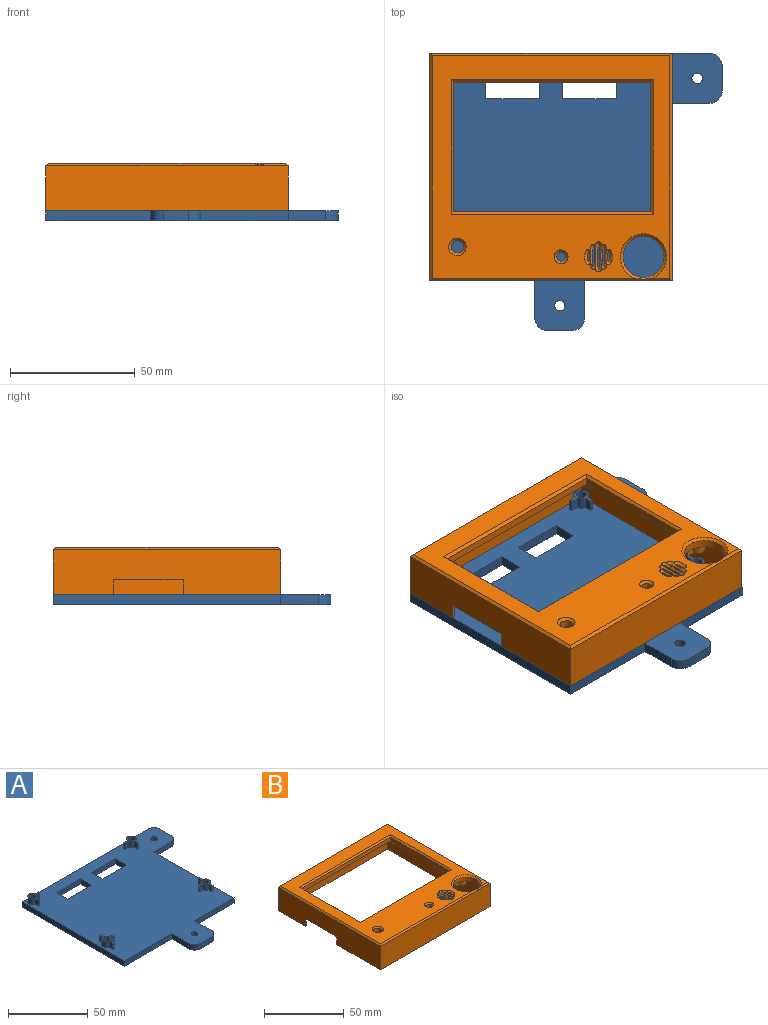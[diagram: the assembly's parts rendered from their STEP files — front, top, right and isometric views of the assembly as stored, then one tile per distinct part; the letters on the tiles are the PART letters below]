
ASSEMBLY  parts=2 mates=1
PART A: 74 faces, bbox 117x111x8.5 mm
  f0: plane 42x4mm, normal (0,-1,0), area 168mm2, adj f22,f57,f62,f65
  f1: plane 71x4mm, normal (1,0,0), area 284mm2, adj f22,f58,f62,f63
  f2: plane 4.5x3.06mm, normal (0,1,0), area 13.8mm2, adj f3,f9,f11,f22
  f3: cylinder r=3mm len=5.94mm, axis (0,0,-1), area 58.2mm2, adj f2,f4,f11,f22
  f4: plane 4.5x3.06mm, normal (-1,0,0), area 13.8mm2, adj f3,f5,f11,f22
  f5: plane 4.5x1.2mm, normal (0,-1,0), area 5.4mm2, adj f4,f6,f11,f22
  f6: plane 4.5x3.06mm, normal (1,0,0), area 13.8mm2, adj f5,f7,f11,f22
  f7: cylinder r=3mm len=4.5mm, axis (0,0,-1), area 15.8mm2, adj f6,f8,f11,f22
  f8: plane 4.5x3.06mm, normal (0,-1,0), area 13.8mm2, adj f7,f9,f11,f22
  f9: plane 4.5x1.2mm, normal (1,0,0), area 5.4mm2, adj f2,f8,f11,f22
  f10: cylinder r=2mm len=8.5mm, axis (0,0,-1), area 106.8mm2, adj f11,f62
  f11: plane 9x9mm, normal (0,0,1), area 23mm2, adj f2,f3,f4,f5,f6,f7,f8,f9
  f12: cylinder r=3mm len=4.5mm, axis (0,0,-1), area 15.8mm2, adj f13,f20,f21,f22
  f13: plane 4.5x3.06mm, normal (-1,0,0), area 13.8mm2, adj f12,f14,f21,f22
  f14: plane 4.5x1.2mm, normal (0,-1,0), area 5.4mm2, adj f13,f15,f21,f22
  f15: plane 4.5x3.06mm, normal (1,0,0), area 13.8mm2, adj f14,f16,f21,f22
  f16: cylinder r=3mm len=5.94mm, axis (0,0,-1), area 58.2mm2, adj f15,f17,f21,f22
  f17: plane 4.5x3.06mm, normal (0,1,0), area 13.8mm2, adj f16,f18,f21,f22
  f18: plane 4.5x1.2mm, normal (-1,0,0), area 5.4mm2, adj f17,f20,f21,f22
  f19: cylinder r=2mm len=8.5mm, axis (0,0,-1), area 106.8mm2, adj f21,f62
  f20: plane 4.5x3.06mm, normal (0,-1,0), area 13.8mm2, adj f12,f18,f21,f22
  f21: plane 9x9mm, normal (0,0,1), area 23mm2, adj f12,f13,f14,f15,f16,f17,f18,f19
  f22: plane 117x111mm, normal (0,0,1), area 8998.5mm2, adj f0,f1,f2,f3,f4,f5,f6,f7
  f23: cylinder r=3mm len=5.88mm, axis (0,0,-1), area 37mm2, adj f22,f24,f35,f36
  f24: plane 4.5x3.06mm, normal (-1,0,0), area 13.8mm2, adj f22,f23,f25,f36
  f25: plane 4.5x1.2mm, normal (0,-1,0), area 5.4mm2, adj f22,f24,f26,f36
  f26: plane 4.5x3.06mm, normal (1,0,0), area 13.8mm2, adj f22,f25,f27,f36
  f27: cylinder r=3mm len=4.5mm, axis (0,0,-1), area 15.8mm2, adj f22,f26,f28,f36
  f28: plane 4.5x3.06mm, normal (0,-1,0), area 13.8mm2, adj f22,f27,f29,f36
  f29: plane 4.5x1.2mm, normal (1,0,0), area 5.4mm2, adj f22,f28,f30,f36
  f30: plane 4.5x3.06mm, normal (0,1,0), area 13.8mm2, adj f22,f29,f31,f36
  f31: cylinder r=3mm len=4.5mm, axis (0,0,-1), area 15.8mm2, adj f22,f30,f32,f36
  f32: plane 4.5x3.06mm, normal (1,0,0), area 13.8mm2, adj f22,f31,f33,f36
  f33: plane 4.5x1.2mm, normal (0,1,0), area 5.4mm2, adj f22,f32,f35,f36
  f34: cylinder r=2mm len=8.5mm, axis (0,0,-1), area 106.8mm2, adj f36,f62
  f35: plane 4.5x3.06mm, normal (-1,0,0), area 13.8mm2, adj f22,f23,f33,f36
  f36: plane 12x9mm, normal (0,0,1), area 26.6mm2, adj f23,f24,f25,f26,f27,f28,f29,f30
  f37: cylinder r=3mm len=4.5mm, axis (0,0,-1), area 15.8mm2, adj f22,f38,f49,f50
  f38: plane 4.5x3.06mm, normal (0,1,0), area 13.8mm2, adj f22,f37,f39,f50
  f39: plane 4.5x1.2mm, normal (-1,0,0), area 5.4mm2, adj f22,f38,f40,f50
  f40: plane 4.5x3.06mm, normal (0,-1,0), area 13.8mm2, adj f22,f39,f41,f50
  f41: cylinder r=3mm len=4.5mm, axis (0,0,-1), area 15.8mm2, adj f22,f40,f42,f50
  f42: plane 4.5x3.06mm, normal (-1,0,0), area 13.8mm2, adj f22,f41,f43,f50
  f43: plane 4.5x1.2mm, normal (0,-1,0), area 5.4mm2, adj f22,f42,f44,f50
  f44: plane 4.5x3.06mm, normal (1,0,0), area 13.8mm2, adj f22,f43,f45,f50
  f45: cylinder r=3mm len=5.88mm, axis (0,0,-1), area 37mm2, adj f22,f44,f46,f50
  f46: plane 4.5x3.06mm, normal (1,0,0), area 13.8mm2, adj f22,f45,f47,f50
  f47: plane 4.5x1.2mm, normal (0,1,0), area 5.4mm2, adj f22,f46,f49,f50
  f48: cylinder r=2mm len=8.5mm, axis (0,0,-1), area 106.8mm2, adj f50,f62
  f49: plane 4.5x3.06mm, normal (-1,0,0), area 13.8mm2, adj f22,f37,f47,f50
  f50: plane 12x9mm, normal (0,0,1), area 26.6mm2, adj f37,f38,f39,f40,f41,f42,f43,f44
  f51: plane 21.5x4mm, normal (0,1,0), area 86mm2, adj f22,f52,f61,f62
  f52: plane 10x4mm, normal (1,0,0), area 40mm2, adj f22,f51,f53,f62
  f53: plane 21.5x4mm, normal (0,-1,0), area 86mm2, adj f22,f52,f61,f62
  f54: plane 21.5x4mm, normal (0,1,0), area 86mm2, adj f22,f55,f59,f62
  f55: plane 10x4mm, normal (1,0,0), area 40mm2, adj f22,f54,f56,f62
  f56: plane 21.5x4mm, normal (0,-1,0), area 86mm2, adj f22,f55,f59,f62
  f57: plane 91x4mm, normal (-1,0,0), area 364mm2, adj f0,f22,f60,f62
  f58: plane 35x4mm, normal (0,-1,0), area 140mm2, adj f1,f22,f62,f66
  f59: plane 10x4mm, normal (-1,0,0), area 40mm2, adj f22,f54,f56,f62
  f60: plane 112x4mm, normal (0,1,0), area 448mm2, adj f22,f57,f62,f73
  f61: plane 10x4mm, normal (-1,0,0), area 40mm2, adj f22,f51,f53,f62
  f62: plane 117x111mm, normal (0,0,-1), area 9097.6mm2, adj f0,f1,f10,f19,f34,f48,f51,f52
  f63: plane 15x4mm, normal (0,-1,0), area 60mm2, adj f1,f22,f62,f72
  f64: plane 10x4mm, normal (1,0,0), area 40mm2, adj f22,f62,f72,f73
  f65: plane 15x4mm, normal (-1,0,0), area 60mm2, adj f0,f22,f62,f71
  f66: plane 15x4mm, normal (1,0,0), area 60mm2, adj f22,f58,f62,f70
  f67: plane 10x4mm, normal (0,-1,0), area 40mm2, adj f22,f62,f70,f71
  f68: cylinder r=2.1mm len=4.2mm, axis (0,0,-1), area 52.8mm2, adj f22,f62
  f69: cylinder r=2.1mm len=4.2mm, axis (0,0,-1), area 52.8mm2, adj f22,f62
  f70: cylinder r=5mm len=5mm, axis (0,0,-1), area 31.4mm2, adj f22,f62,f66,f67
  f71: cylinder r=5mm len=5mm, axis (0,0,1), area 31.4mm2, adj f22,f62,f65,f67
  f72: cylinder r=5mm len=5mm, axis (0,0,1), area 31.4mm2, adj f22,f62,f63,f64
  f73: cylinder r=5mm len=5mm, axis (0,0,-1), area 31.4mm2, adj f22,f60,f62,f64
PART B: 86 faces, bbox 98.1x92.1x20.1 mm
  f0: plane 91x18mm, normal (-1,0,0), area 1470mm2, adj f1,f3,f17,f67,f68,f69,f79
  f1: plane 97x91mm, normal (0,0,-1), area 411.8mm2, adj f0,f3,f4,f17,f19,f20,f21,f22
  f2: plane 94.6x88.6mm, normal (0,0,-1), area 3858.5mm2, adj f5,f6,f7,f8,f9,f10,f11,f12
  f3: plane 97x18mm, normal (0,-1,0), area 1746mm2, adj f0,f1,f4,f80
  f4: plane 91x18mm, normal (1,0,0), area 1638mm2, adj f1,f3,f17,f78
  f5: plane 79x3mm, normal (0,1,0), area 237mm2, adj f2,f6,f8,f84
  f6: plane 52x3mm, normal (1,0,0), area 156mm2, adj f2,f5,f7,f82
  f7: plane 79x3mm, normal (0,-1,0), area 237mm2, adj f2,f6,f8,f83
  f8: plane 52x3mm, normal (-1,0,0), area 156mm2, adj f2,f5,f7,f85
  f9: cylinder r=8.25mm len=16.5mm, axis (0,0,-1), area 155.5mm2, adj f2,f81
  f10: extruded ~10x3mm, area 61.3mm2, adj f2,f74
  f11: extruded ~8x3mm, area 49.4mm2, adj f2,f73
  f12: extruded ~4x3mm, area 26mm2, adj f2,f72
  f13: extruded ~8x3mm, area 49.4mm2, adj f2,f75
  f14: extruded ~4x3mm, area 26mm2, adj f2,f76
  f15: cylinder r=1.8mm len=3.6mm, axis (0,0,-1), area 33.9mm2, adj f2,f71
  f16: cylinder r=2.5mm len=5mm, axis (0,0,-1), area 47.1mm2, adj f2,f70
  f17: plane 97x18mm, normal (0,1,0), area 1746mm2, adj f0,f1,f4,f77
  f18: plane 95.18x89.18mm, normal (0,0,1), area 3661.8mm2, adj f70,f71,f72,f73,f74,f75,f76,f77
  f19: plane 94.6x15mm, normal (0,1,0), area 1419mm2, adj f1,f2,f20,f22
  f20: plane 88.6x15mm, normal (-1,0,0), area 1329mm2, adj f1,f2,f19,f21
  f21: plane 94.6x15mm, normal (0,-1,0), area 1419mm2, adj f1,f2,f20,f22
  f22: plane 88.6x15mm, normal (1,0,0), area 1161mm2, adj f1,f2,f19,f21,f67,f68,f69
  f23: cylinder r=3mm len=4.5mm, axis (0,0,1), area 15.8mm2, adj f2,f24,f31,f32
  f24: plane 4.5x3.06mm, normal (0,-1,0), area 13.8mm2, adj f2,f23,f25,f32
  f25: plane 4.5x1.2mm, normal (-1,0,0), area 5.4mm2, adj f2,f24,f26,f32
  f26: plane 4.5x3.06mm, normal (0,1,0), area 13.8mm2, adj f2,f25,f27,f32
  f27: cylinder r=3mm len=5.94mm, axis (0,0,1), area 58.2mm2, adj f2,f26,f28,f32
  f28: plane 4.5x3.06mm, normal (1,0,0), area 13.8mm2, adj f2,f27,f29,f32
  f29: plane 4.5x1.2mm, normal (0,-1,0), area 5.4mm2, adj f2,f28,f31,f32
  f30: cylinder r=1.4mm len=6.9mm, axis (0,0,1), area 60.7mm2, adj f32,f66
  f31: plane 4.5x3.06mm, normal (-1,0,0), area 13.8mm2, adj f2,f23,f29,f32
  f32: plane 9x9mm, normal (0,0,-1), area 29.4mm2, adj f23,f24,f25,f26,f27,f28,f29,f30
  f33: cylinder r=3mm len=4.5mm, axis (0,0,1), area 15.8mm2, adj f2,f34,f41,f42
  f34: plane 4.5x3.06mm, normal (1,0,0), area 13.8mm2, adj f2,f33,f35,f42
  f35: plane 4.5x1.2mm, normal (0,-1,0), area 5.4mm2, adj f2,f34,f36,f42
  f36: plane 4.5x3.06mm, normal (-1,0,0), area 13.8mm2, adj f2,f35,f37,f42
  f37: cylinder r=3mm len=5.94mm, axis (0,0,1), area 58.2mm2, adj f2,f36,f38,f42
  f38: plane 4.5x3.06mm, normal (0,1,0), area 13.8mm2, adj f2,f37,f39,f42
  f39: plane 4.5x1.2mm, normal (1,0,0), area 5.4mm2, adj f2,f38,f41,f42
  f40: cylinder r=1.4mm len=6.9mm, axis (0,0,1), area 60.7mm2, adj f42,f65
  f41: plane 4.5x3.06mm, normal (0,-1,0), area 13.8mm2, adj f2,f33,f39,f42
  f42: plane 9x9mm, normal (0,0,-1), area 29.4mm2, adj f33,f34,f35,f36,f37,f38,f39,f40
  f43: plane 4.5x3.06mm, normal (0,-1,0), area 13.8mm2, adj f2,f44,f50,f52
  f44: cylinder r=3mm len=5.94mm, axis (0,0,1), area 58.2mm2, adj f2,f43,f45,f52
  f45: plane 4.5x3.06mm, normal (-1,0,0), area 13.8mm2, adj f2,f44,f46,f52
  f46: plane 4.5x1.2mm, normal (0,1,0), area 5.4mm2, adj f2,f45,f47,f52
  f47: plane 4.5x3.06mm, normal (1,0,0), area 13.8mm2, adj f2,f46,f48,f52
  f48: cylinder r=3mm len=4.5mm, axis (0,0,1), area 15.8mm2, adj f2,f47,f49,f52
  f49: plane 4.5x3.06mm, normal (0,1,0), area 13.8mm2, adj f2,f48,f50,f52
  f50: plane 4.5x1.2mm, normal (1,0,0), area 5.4mm2, adj f2,f43,f49,f52
  f51: cylinder r=1.4mm len=6.9mm, axis (0,0,1), area 60.7mm2, adj f52,f64
  f52: plane 9x9mm, normal (0,0,-1), area 29.4mm2, adj f43,f44,f45,f46,f47,f48,f49,f50
  f53: cylinder r=3mm len=4.5mm, axis (0,0,1), area 15.8mm2, adj f2,f54,f61,f62
  f54: plane 4.5x3.06mm, normal (-1,0,0), area 13.8mm2, adj f2,f53,f55,f62
  f55: plane 4.5x1.2mm, normal (0,1,0), area 5.4mm2, adj f2,f54,f56,f62
  f56: plane 4.5x3.06mm, normal (1,0,0), area 13.8mm2, adj f2,f55,f57,f62
  f57: cylinder r=3mm len=5.94mm, axis (0,0,1), area 58.2mm2, adj f2,f56,f58,f62
  f58: plane 4.5x3.06mm, normal (0,-1,0), area 13.8mm2, adj f2,f57,f59,f62
  f59: plane 4.5x1.2mm, normal (-1,0,0), area 5.4mm2, adj f2,f58,f61,f62
  f60: cylinder r=1.4mm len=6.9mm, axis (0,0,1), area 60.7mm2, adj f62,f63
  f61: plane 4.5x3.06mm, normal (0,1,0), area 13.8mm2, adj f2,f53,f59,f62
  f62: plane 9x9mm, normal (0,0,-1), area 29.4mm2, adj f53,f54,f55,f56,f57,f58,f59,f60
  f63: plane 2.8x2.8mm, normal (0,0,-1), area 6.2mm2, adj f60
  f64: plane 2.8x2.8mm, normal (0,0,-1), area 6.2mm2, adj f51
  f65: plane 2.8x2.8mm, normal (0,0,-1), area 6.2mm2, adj f40
  f66: plane 2.8x2.8mm, normal (0,0,-1), area 6.2mm2, adj f30
  f67: plane 28x1.2mm, normal (0,0,-1), area 33.6mm2, adj f0,f22,f68,f69
  f68: plane 6x1.2mm, normal (0,1,0), area 7.2mm2, adj f0,f1,f22,f67
  f69: plane 6x1.2mm, normal (0,-1,0), area 7.2mm2, adj f0,f1,f22,f67
  f70: cone r=2.5mm half-angle=45deg, axis (0,0,1), area 26.7mm2, adj f16,f18
  f71: cone r=1.8mm half-angle=45deg, axis (0,0,1), area 20.4mm2, adj f15,f18
  f72: bspline ~5.99x3.1mm, area 13.3mm2, adj f12,f18,f73
  f73: bspline ~9.98x3.1mm, area 18.9mm2, adj f11,f18,f72,f74
  f74: bspline ~11.97x3.1mm, area 22.2mm2, adj f10,f18,f73,f75
  f75: bspline ~9.98x3.1mm, area 18.9mm2, adj f13,f18,f74,f76
  f76: bspline ~5.99x3.1mm, area 13.3mm2, adj f14,f18,f75
  f77: plane 97x1mm, normal (0,0.71,0.71), area 135.8mm2, adj f17,f18,f78,f79
  f78: plane 91x1mm, normal (0.71,0,0.71), area 127.3mm2, adj f4,f18,f77,f80
  f79: plane 91x1mm, normal (-0.71,0,0.71), area 127.3mm2, adj f0,f18,f77,f80
  f80: plane 98.06x2.06mm, normal (0,-0.71,0.71), area 133.2mm2, adj f3,f18,f78,f79,f81
  f81: cone r=8.25mm half-angle=45deg, axis (0,0,1), area 77.8mm2, adj f9,f18,f80
  f82: plane 54x1mm, normal (0.71,0,0.71), area 75mm2, adj f6,f18,f83,f84
  f83: plane 81x1mm, normal (0,-0.71,0.71), area 113.1mm2, adj f7,f18,f82,f85
  f84: plane 81x1mm, normal (0,0.71,0.71), area 113.1mm2, adj f5,f18,f82,f85
  f85: plane 54x1mm, normal (-0.71,0,0.71), area 75mm2, adj f8,f18,f83,f84
PLACE A t=(91.39,-6.91,-12.81)mm
PLACE B t=(-41.83,-5.79,2.19)mm
MATE fastened A.f12 <-> B.f23  axis (0,0,1) through (16.59,25.15,-8.31)mm
